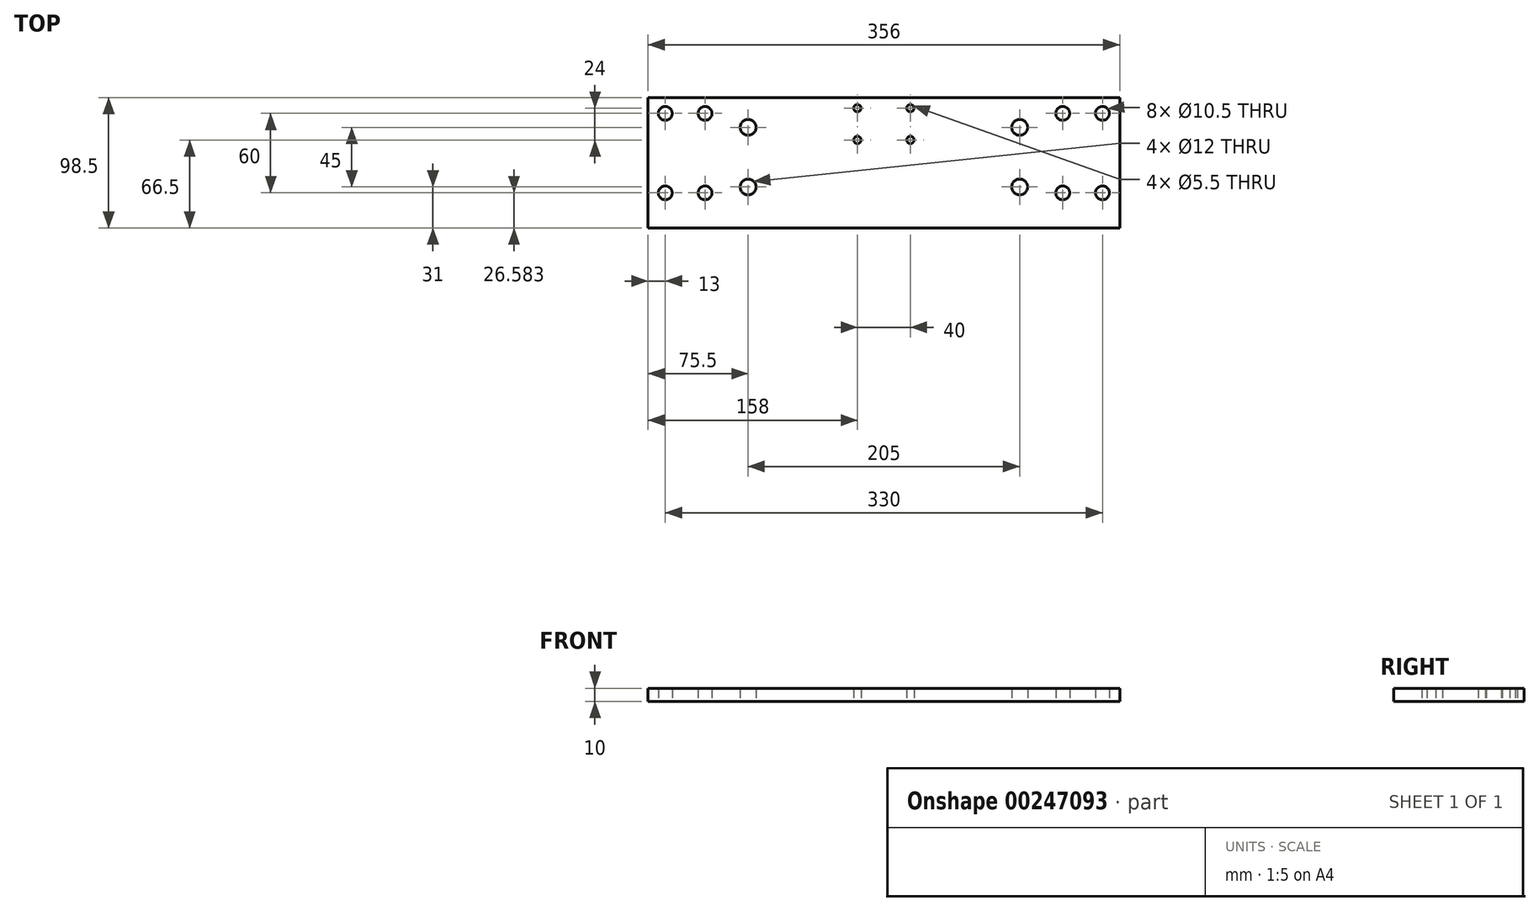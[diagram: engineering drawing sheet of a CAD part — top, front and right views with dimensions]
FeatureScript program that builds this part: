
annotation { "Feature Type Name" : "Feature", "Feature Type Description" : "" }
export const myFeature = defineFeature(function(context is Context, id is Id, definition is map)
    precondition{}
    {
        {
            var Q0;
            Q0=qCreatedBy(makeId("Top.planeOp"),FACE);
            var sketch = newSketch(context, id + "F0", { "sketchPlane" : qUnion([Q0])});
            skLineSegment(sketch, "E0.bottom", {"start": v(0, 0) * mm, "end": v(356, 0) * mm});
            skLineSegment(sketch, "E0.top", {"start": v(0, -98.5) * mm, "end": v(356, -98.5) * mm});
            skLineSegment(sketch, "E0.left", {"start": v(0, 0) * mm, "end": v(0, -98.5) * mm});
            skLineSegment(sketch, "E0.right", {"start": v(356, 0) * mm, "end": v(356, -98.5) * mm});
            skLineSegment(sketch, "E1", {"start": v(178, 0) * mm, "end": v(178, -98.5) * mm, "construction": true});
            skPoint(sketch, "E2", {"position": v(43, -11.92) * mm});
            skPoint(sketch, "E3.0.1.0", {"position": v(43, -71.92) * mm});
            skPoint(sketch, "E3.1.0.0", {"position": v(13, -11.92) * mm});
            skPoint(sketch, "E3.1.1.0", {"position": v(13, -71.92) * mm});
            skLineSegment(sketch, "E3.direction1", {"start": v(43, -11.92) * mm, "end": v(13, -11.92) * mm, "construction": true});
            skLineSegment(sketch, "E3.direction2", {"start": v(43, -11.92) * mm, "end": v(43, -71.92) * mm, "construction": true});
            skPoint(sketch, "E4.MirrorP", {"position": v(343, -11.92) * mm});
            skPoint(sketch, "E5.MirrorP", {"position": v(313, -11.92) * mm});
            skPoint(sketch, "E6.MirrorP", {"position": v(313, -71.92) * mm});
            skPoint(sketch, "E7.MirrorP", {"position": v(343, -71.92) * mm});
            skSolve(sketch);
        }
        {
            var Q0;
            Q0=makeQuery(id+"F0.imprint","IMPRINT",FACE,{"disambiguationData":[TD([[makeQuery(id+"F0.imprint","IMPRINT",EDGE,{"derivedFrom":sQuery(id+"F0.wireOp",EDGE,"E0.bottom")}),-1.0]])]});
            var sketch = newSketch(context, id + "F1", { "sketchPlane" : qUnion([Q0])});
            skPoint(sketch, "E8", {"position": v(75.5, -22.5) * mm});
            skPoint(sketch, "E9.0.1.0", {"position": v(75.5, -67.5) * mm});
            skLineSegment(sketch, "E9.direction1", {"start": v(75.5, -22.5) * mm, "end": v(100.5, -22.5) * mm, "construction": true});
            skLineSegment(sketch, "E9.direction2", {"start": v(75.5, -22.5) * mm, "end": v(75.5, -67.5) * mm, "construction": true});
            skPoint(sketch, "E10.MirrorP", {"position": v(280.5, -67.5) * mm});
            skPoint(sketch, "E11.MirrorP", {"position": v(280.5, -22.5) * mm});
            skSolve(sketch);
        }
        {
            var Q0;
            Q0=qCreatedBy(makeId("Top.planeOp"),FACE);
            var sketch = newSketch(context, id + "F2", { "sketchPlane" : qUnion([Q0])});
            skPoint(sketch, "E12", {"position": v(158, -8) * mm});
            skPoint(sketch, "E13", {"position": v(158, -32) * mm});
            skPoint(sketch, "E14.MirrorP", {"position": v(198, -8) * mm});
            skPoint(sketch, "E15.MirrorP", {"position": v(198, -32) * mm});
            skSolve(sketch);
        }
        {
            var Q0;
            Q0=makeQuery(id+"F0.imprint","IMPRINT",FACE,{"disambiguationData":[TD([[makeQuery(id+"F0.imprint","IMPRINT",EDGE,{"derivedFrom":sQuery(id+"F0.wireOp",EDGE,"E0.bottom")}),-1.0]])]});
            extrude(context, id + "F3", {"entities" : qUnion([Q0]), "depth" : 10 * mm, "offsetDistance" : 25 * mm});
        }
        {
            var Q0;
            Q0=sQuery(id+"F1.wireOp",VERTEX,"E8");
            var Q1;
            Q1=sQuery(id+"F1.wireOp",VERTEX,"E9.0.1.0");
            var Q2;
            Q2=sQuery(id+"F1.wireOp",VERTEX,"E10.MirrorP");
            var Q3;
            Q3=sQuery(id+"F1.wireOp",VERTEX,"E11.MirrorP");
            var Q4;
            Q4=makeQuery(id+"F3.opExtrude","SWEPT_BODY",BODY,{"disambiguationData":[OSD([sQuery(id+"F0.wireOp",EDGE,"E0.bottom"),sQuery(id+"F0.wireOp",EDGE,"E0.top"),sQuery(id+"F0.wireOp",EDGE,"E0.left"),sQuery(id+"F0.wireOp",EDGE,"E0.right")])]});
            hole(context, id + "F4", {"style" : HoleStyle.SIMPLE, "endStyle" : HoleEndStyle.THROUGH, "oppositeDirection" : true, "holeDiameter" : 12 * mm, "majorDiameter" : 5 * mm, "isTappedThrough" : true, "tappedDepth" : 12 * mm, "tapClearance" : 3, "locations" : qUnion([Q0, Q1, Q2, Q3]), "scope" : qUnion([Q4])});
        }
        {
            var Q0;
            Q0=sQuery(id+"F0.wireOp",VERTEX,"E3.1.0.0");
            var Q1;
            Q1=sQuery(id+"F0.wireOp",VERTEX,"E2");
            var Q2;
            Q2=sQuery(id+"F0.wireOp",VERTEX,"E3.1.1.0");
            var Q3;
            Q3=sQuery(id+"F0.wireOp",VERTEX,"E3.0.1.0");
            var Q4;
            Q4=sQuery(id+"F0.wireOp",VERTEX,"E5.MirrorP");
            var Q5;
            Q5=sQuery(id+"F0.wireOp",VERTEX,"E4.MirrorP");
            var Q6;
            Q6=sQuery(id+"F0.wireOp",VERTEX,"E7.MirrorP");
            var Q7;
            Q7=sQuery(id+"F0.wireOp",VERTEX,"E6.MirrorP");
            var Q8;
            Q8=makeQuery(id+"F3.opExtrude","SWEPT_BODY",BODY,{"disambiguationData":[OSD([sQuery(id+"F0.wireOp",EDGE,"E0.bottom"),sQuery(id+"F0.wireOp",EDGE,"E0.top"),sQuery(id+"F0.wireOp",EDGE,"E0.left"),sQuery(id+"F0.wireOp",EDGE,"E0.right")])]});
            hole(context, id + "F5", {"style" : HoleStyle.SIMPLE, "endStyle" : HoleEndStyle.THROUGH, "oppositeDirection" : true, "holeDiameter" : 10.5 * mm, "majorDiameter" : 5 * mm, "isTappedThrough" : true, "tappedDepth" : 12 * mm, "tapClearance" : 3, "locations" : qUnion([Q0, Q1, Q2, Q3, Q4, Q5, Q6, Q7]), "scope" : qUnion([Q8])});
        }
        {
            var Q0;
            Q0=sQuery(id+"F2.wireOp",VERTEX,"E12");
            var Q1;
            Q1=sQuery(id+"F2.wireOp",VERTEX,"E14.MirrorP");
            var Q2;
            Q2=sQuery(id+"F2.wireOp",VERTEX,"E13");
            var Q3;
            Q3=sQuery(id+"F2.wireOp",VERTEX,"E15.MirrorP");
            var Q4;
            Q4=makeQuery(id+"F3.opExtrude","SWEPT_BODY",BODY,{"disambiguationData":[OSD([sQuery(id+"F0.wireOp",EDGE,"E0.bottom"),sQuery(id+"F0.wireOp",EDGE,"E0.top"),sQuery(id+"F0.wireOp",EDGE,"E0.left"),sQuery(id+"F0.wireOp",EDGE,"E0.right")])]});
            hole(context, id + "F6", {"style" : HoleStyle.SIMPLE, "endStyle" : HoleEndStyle.THROUGH, "oppositeDirection" : true, "holeDiameter" : 5.5 * mm, "majorDiameter" : 5 * mm, "isTappedThrough" : true, "tappedDepth" : 12 * mm, "tapClearance" : 3, "locations" : qUnion([Q0, Q1, Q2, Q3]), "scope" : qUnion([Q4])});
        }
    });
